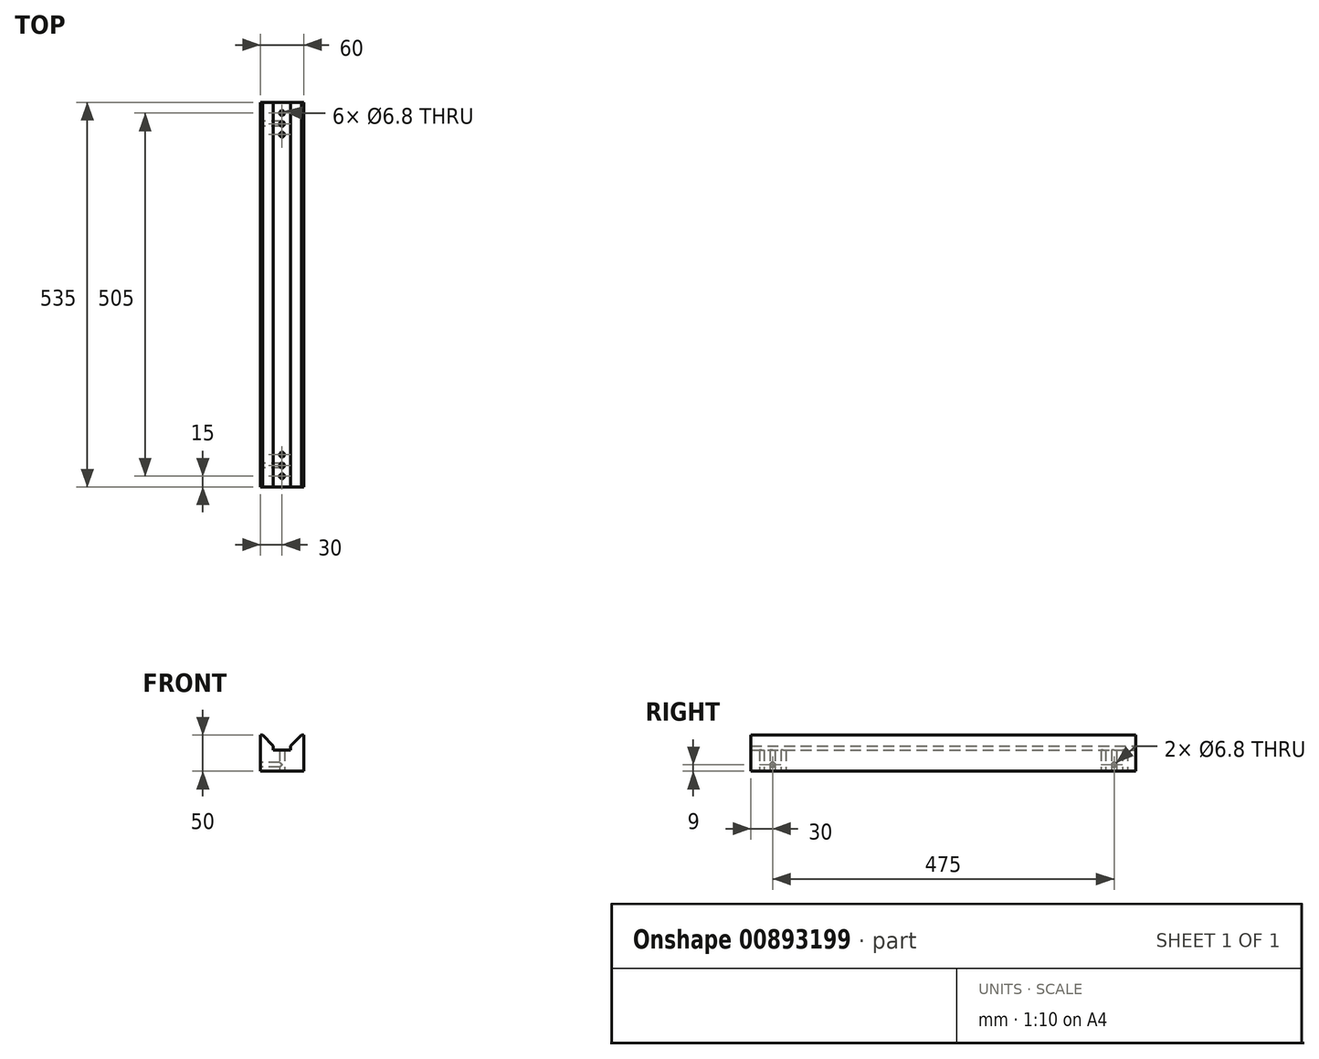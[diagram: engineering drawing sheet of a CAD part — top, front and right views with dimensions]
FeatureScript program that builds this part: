
annotation { "Feature Type Name" : "Feature", "Feature Type Description" : "" }
export const myFeature = defineFeature(function(context is Context, id is Id, definition is map)
    precondition{}
    {
        {
            var Q0;
            Q0=qCreatedBy(makeId("Front.planeOp"),FACE);
            var sketch = newSketch(context, id + "F0", { "sketchPlane" : qUnion([Q0])});
            skLineSegment(sketch, "E0", {"start": v(0, 0) * mm, "end": v(60, 0) * mm});
            skLineSegment(sketch, "E1", {"start": v(60, 0) * mm, "end": v(60, 50) * mm});
            skLineSegment(sketch, "E2", {"start": v(60, 50) * mm, "end": v(57, 50) * mm});
            skLineSegment(sketch, "E3", {"start": v(0, 0) * mm, "end": v(0, 50) * mm});
            skLineSegment(sketch, "E4", {"start": v(0, 50) * mm, "end": v(3, 50) * mm});
            skLineSegment(sketch, "E5", {"start": v(30, 29) * mm, "end": v(18, 29) * mm});
            skLineSegment(sketch, "E6", {"start": v(18, 29) * mm, "end": v(18, 35) * mm});
            skLineSegment(sketch, "E7", {"start": v(18, 35) * mm, "end": v(3, 50) * mm});
            skLineSegment(sketch, "E8.MirrorCS", {"start": v(42, 35) * mm, "end": v(57, 50) * mm});
            skLineSegment(sketch, "E9.MirrorCS", {"start": v(42, 29) * mm, "end": v(42, 35) * mm});
            skLineSegment(sketch, "E10.MirrorCS", {"start": v(30, 29) * mm, "end": v(42, 29) * mm});
            skSolve(sketch);
        }
        {
            var Q0;
            Q0=makeQuery(id+"F0.imprint","IMPRINT",FACE,{"disambiguationData":[TD([[makeQuery(id+"F0.imprint","IMPRINT",EDGE,{"derivedFrom":sQuery(id+"F0.wireOp",EDGE,"E0")}),1.0]])]});
            extrude(context, id + "F1", {"entities" : qUnion([Q0]), "depth" : 535 * mm, "offsetDistance" : 25 * mm});
        }
        {
            var Q0;
            Q0=makeQuery(id+"F1.opExtrude","SWEPT_FACE",FACE,{"disambiguationData":[OSD([sQuery(id+"F0.wireOp",EDGE,"E0")])]});
            var sketch = newSketch(context, id + "F2", { "sketchPlane" : qUnion([Q0])});
            skCircle(sketch, "E11", {"center": v(30, 520) * mm, "radius": 3.4 * mm});
            skCircle(sketch, "E12", {"center": v(30, 505) * mm, "radius": 3.4 * mm});
            skCircle(sketch, "E13", {"center": v(30, 490) * mm, "radius": 3.4 * mm});
            skCircle(sketch, "E14", {"center": v(30, 15) * mm, "radius": 3.4 * mm});
            skCircle(sketch, "E15", {"center": v(30, 30) * mm, "radius": 3.4 * mm});
            skCircle(sketch, "E16", {"center": v(30, 45) * mm, "radius": 3.4 * mm});
            skSolve(sketch);
        }
        {
            var Q0;
            Q0=makeQuery(id+"F2.imprint","IMPRINT",FACE,{"disambiguationData":[TD([[makeQuery(id+"F2.imprint","IMPRINT",EDGE,{"derivedFrom":sQuery(id+"F2.wireOp",EDGE,"E11")}),1.0]])]});
            var Q1;
            Q1=makeQuery(id+"F2.imprint","IMPRINT",FACE,{"disambiguationData":[TD([[makeQuery(id+"F2.imprint","IMPRINT",EDGE,{"derivedFrom":sQuery(id+"F2.wireOp",EDGE,"E12")}),1.0]])]});
            var Q2;
            Q2=makeQuery(id+"F2.imprint","IMPRINT",FACE,{"disambiguationData":[TD([[makeQuery(id+"F2.imprint","IMPRINT",EDGE,{"derivedFrom":sQuery(id+"F2.wireOp",EDGE,"E13")}),1.0]])]});
            var Q3;
            Q3=makeQuery(id+"F2.imprint","IMPRINT",FACE,{"disambiguationData":[TD([[makeQuery(id+"F2.imprint","IMPRINT",EDGE,{"derivedFrom":sQuery(id+"F2.wireOp",EDGE,"E16")}),1.0]])]});
            var Q4;
            Q4=makeQuery(id+"F2.imprint","IMPRINT",FACE,{"disambiguationData":[TD([[makeQuery(id+"F2.imprint","IMPRINT",EDGE,{"derivedFrom":sQuery(id+"F2.wireOp",EDGE,"E15")}),1.0]])]});
            var Q5;
            Q5=makeQuery(id+"F2.imprint","IMPRINT",FACE,{"disambiguationData":[TD([[makeQuery(id+"F2.imprint","IMPRINT",EDGE,{"derivedFrom":sQuery(id+"F2.wireOp",EDGE,"E14")}),1.0]])]});
            extrude(context, id + "F3", {"entities" : qUnion([Q0, Q1, Q2, Q3, Q4, Q5]), "operationType" : NewBodyOperationType.REMOVE, "oppositeDirection" : true, "depth" : 30 * mm, "offsetDistance" : 25 * mm});
        }
        {
            var Q0;
            Q0=makeQuery(id+"F1.opExtrude","SWEPT_FACE",FACE,{"disambiguationData":[OSD([sQuery(id+"F0.wireOp",EDGE,"E3")])]});
            var sketch = newSketch(context, id + "F4", { "sketchPlane" : qUnion([Q0])});
            skCircle(sketch, "E17", {"center": v(30, 9) * mm, "radius": 3.4 * mm});
            skCircle(sketch, "E18", {"center": v(505, 9) * mm, "radius": 3.4 * mm});
            skSolve(sketch);
        }
        {
            var Q0;
            Q0=makeQuery(id+"F4.imprint","IMPRINT",FACE,{"disambiguationData":[TD([[makeQuery(id+"F4.imprint","IMPRINT",EDGE,{"derivedFrom":sQuery(id+"F4.wireOp",EDGE,"E17")}),1.0]])]});
            var Q1;
            Q1=makeQuery(id+"F4.imprint","IMPRINT",FACE,{"disambiguationData":[TD([[makeQuery(id+"F4.imprint","IMPRINT",EDGE,{"derivedFrom":sQuery(id+"F4.wireOp",EDGE,"E18")}),1.0]])]});
            extrude(context, id + "F5", {"entities" : qUnion([Q0, Q1]), "operationType" : NewBodyOperationType.REMOVE, "oppositeDirection" : true, "depth" : 30 * mm, "offsetDistance" : 25 * mm});
        }
    });
